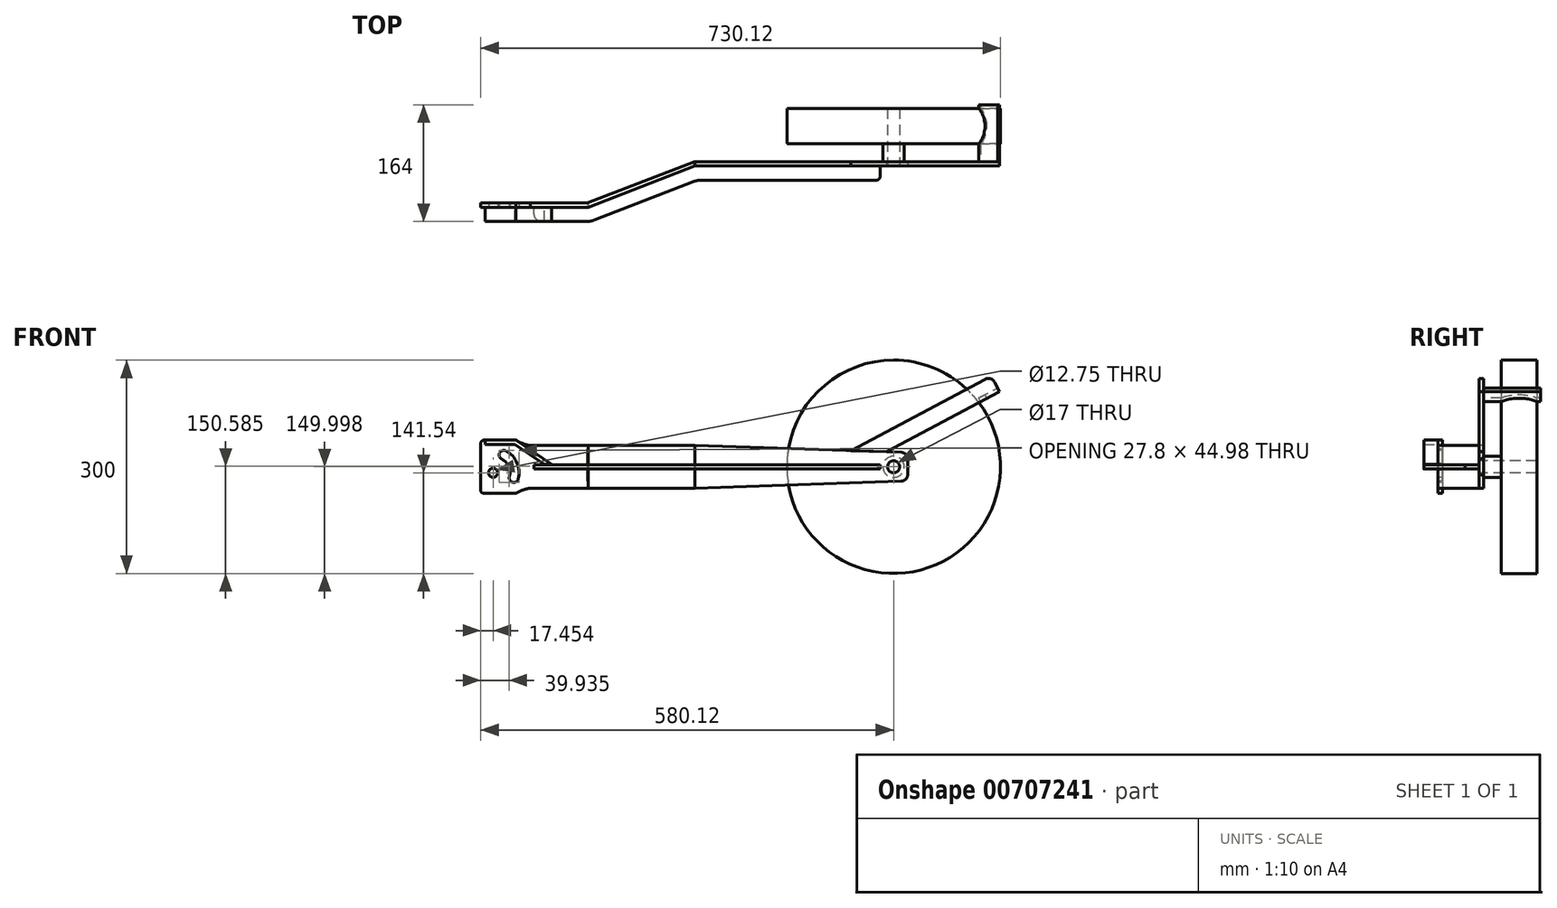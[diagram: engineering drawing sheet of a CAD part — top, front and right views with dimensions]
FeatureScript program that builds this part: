
annotation { "Feature Type Name" : "Feature", "Feature Type Description" : "" }
export const myFeature = defineFeature(function(context is Context, id is Id, definition is map)
    precondition{}
    {
        {
            var Q0;
            Q0=qCreatedBy(makeId("Top.planeOp"),FACE);
            var sketch = newSketch(context, id + "F0", { "sketchPlane" : qUnion([Q0])});
            skLineSegment(sketch, "E0", {"start": v(-300, 0) * mm, "end": v(300, 0) * mm, "construction": true});
            skLineSegment(sketch, "E1", {"start": v(-300, 0) * mm, "end": v(-150, 0) * mm});
            skLineSegment(sketch, "E2", {"start": v(-150, 0) * mm, "end": v(0, 58) * mm});
            skLineSegment(sketch, "E3", {"start": v(0, 58) * mm, "end": v(300, 58) * mm});
            skLineSegment(sketch, "E4", {"start": v(-300, 0) * mm, "end": v(-300, 128) * mm, "construction": true});
            skLineSegment(sketch, "E5", {"start": v(300, 0) * mm, "end": v(300, 128.18) * mm, "construction": true});
            skLineSegment(sketch, "E6.0", {"start": v(1.12, 52) * mm, "end": v(300.12, 52) * mm});
            skLineSegment(sketch, "E6.1", {"start": v(-148.88, -6) * mm, "end": v(1.12, 52) * mm});
            skLineSegment(sketch, "E6.2", {"start": v(-300, -6) * mm, "end": v(-148.88, -6) * mm});
            skLineSegment(sketch, "E7", {"start": v(-300, 0) * mm, "end": v(-300, -6) * mm});
            skLineSegment(sketch, "E8", {"start": v(300, 58) * mm, "end": v(300.12, 52) * mm});
            skLineSegment(sketch, "E9", {"start": v(-300, 33.9) * mm, "end": v(-300, 101.04) * mm});
            skSolve(sketch);
        }
        {
            var Q0;
            Q0 = qSketchRegion(id + "F0", true);
            extrude(context, id + "F1", {"entities" : qUnion([Q0]), "depth" : 60 * mm, "offsetDistance" : 25 * mm});
        }
        {
            var Q0;
            Q0=makeQuery(id+"F1.opExtrude","SWEPT_FACE",FACE,{"disambiguationData":[OSD([sQuery(id+"F0.wireOp",EDGE,"E6.2")])]});
            var sketch = newSketch(context, id + "F2", { "sketchPlane" : qUnion([Q0])});
            skLineSegment(sketch, "E10", {"start": v(-295, 67.5) * mm, "end": v(-250.3, 67.5) * mm});
            skPoint(sketch, "E11.visualSharp", {"position": v(-225, 67.5) * mm});
            skPoint(sketch, "E12.visualSharp", {"position": v(-225, -7.5) * mm});
            skPoint(sketch, "E13.visualSharp", {"position": v(-306, 67.5) * mm});
            skPoint(sketch, "E14.visualSharp", {"position": v(-300, -7.5) * mm});
            skPoint(sketch, "E15", {"position": v(-230, 60) * mm});
            skArc(sketch, "E16", {"start": v(-250.3, 67.5) * mm, "mid": v(-240.6, 62.51) * mm, "end": v(-230, 60) * mm});
            skPoint(sketch, "E17", {"position": v(-230, 0) * mm});
            skLineSegment(sketch, "E18", {"start": v(-230, 60) * mm, "end": v(-230, 0) * mm});
            skLineSegment(sketch, "E19", {"start": v(-148.88, 30) * mm, "end": v(-148.88, 30) * mm});
            skPoint(sketch, "E20.newPointA", {"position": v(-300, 67.5) * mm});
            skPoint(sketch, "E20.newPointB", {"position": v(-315.3, 67.5) * mm});
            skArc(sketch, "E20.filletArc", {"start": v(-295, 67.5) * mm, "mid": v(-298.54, 66.04) * mm, "end": v(-300, 62.5) * mm});
            skLineSegment(sketch, "E21", {"start": v(-240.6, 62.51) * mm, "end": v(-240.6, 0) * mm, "construction": true});
            skLineSegment(sketch, "E22.0", {"start": v(-300, 60) * mm, "end": v(-300, 0) * mm});
            skLineSegment(sketch, "E23", {"start": v(-300, 60) * mm, "end": v(-300, 62.5) * mm});
            skLineSegment(sketch, "E24", {"start": v(-300, 30) * mm, "end": v(-187.15, 30) * mm, "construction": true});
            skLineSegment(sketch, "E25.MirrorCS", {"start": v(-295, -7.5) * mm, "end": v(-250.3, -7.5) * mm});
            skArc(sketch, "E26.MirrorCS", {"start": v(-250.3, -7.5) * mm, "mid": v(-240.6, -2.51) * mm, "end": v(-230, 0) * mm});
            skArc(sketch, "E27.MirrorCS", {"start": v(-295, -7.5) * mm, "mid": v(-298.54, -6.04) * mm, "end": v(-300, -2.5) * mm});
            skLineSegment(sketch, "E28.MirrorCS", {"start": v(-300, 0) * mm, "end": v(-300, -2.5) * mm});
            skSolve(sketch);
        }
        {
            var Q0;
            Q0=makeQuery(id+"F1.opExtrude","SWEPT_FACE",FACE,{"disambiguationData":[OSD([sQuery(id+"F0.wireOp",EDGE,"E6.0")])]});
            var sketch = newSketch(context, id + "F3", { "sketchPlane" : qUnion([Q0])});
            skCircle(sketch, "E29", {"center": v(280.12, 30) * mm, "radius": 8.25 * mm});
            skPoint(sketch, "E29.centerSnap0", {"position": v(300.7, 30) * mm});
            skLineSegment(sketch, "E30", {"start": v(1.12, 60) * mm, "end": v(290.45, 50.32) * mm});
            skLineSegment(sketch, "E31", {"start": v(1.12, 0) * mm, "end": v(290.45, 9.68) * mm});
            skLineSegment(sketch, "E32", {"start": v(300.12, 40.33) * mm, "end": v(300.12, 19.67) * mm});
            skPoint(sketch, "E33.visualSharp", {"position": v(300.12, 50) * mm});
            skArc(sketch, "E33.filletArc", {"start": v(300.12, 40.33) * mm, "mid": v(297.3, 47.28) * mm, "end": v(290.45, 50.32) * mm});
            skPoint(sketch, "E34.visualSharp", {"position": v(300.12, 10) * mm});
            skArc(sketch, "E34.filletArc", {"start": v(290.45, 9.68) * mm, "mid": v(297.3, 12.72) * mm, "end": v(300.12, 19.67) * mm});
            skSolve(sketch);
        }
        {
            var Q0;
            {var subQ0=sQuery(id+"F3.wireOp",EDGE,"E30");Q0=makeQuery(id+"F3.imprint","IMPRINT",FACE,{"disambiguationData":[TD([[makeQuery(id+"F3.imprint","IMPRINT",EDGE,{"derivedFrom":subQ0}),1.0]])]});}
            var Q1;
            {var subQ0=sQuery(id+"F3.wireOp",EDGE,"E31");Q1=makeQuery(id+"F3.imprint","IMPRINT",FACE,{"disambiguationData":[TD([[makeQuery(id+"F3.imprint","IMPRINT",EDGE,{"derivedFrom":subQ0}),-1.0]])]});}
            var Q2;
            Q2=makeQuery(id+"F3.imprint","IMPRINT",FACE,{"disambiguationData":[TD([[makeQuery(id+"F3.imprint","IMPRINT",EDGE,{"derivedFrom":sQuery(id+"F3.wireOp",EDGE,"E29")}),1.0]])]});
            extrude(context, id + "F4", {"entities" : qUnion([Q0, Q1, Q2]), "operationType" : NewBodyOperationType.REMOVE, "oppositeDirection" : true, "depth" : 25 * mm, "offsetDistance" : 25 * mm});
        }
        {
            var Q0;
            Q0=makeQuery(id+"F2.imprint","IMPRINT",FACE,{"disambiguationData":[TD([[makeQuery(id+"F2.imprint","IMPRINT",EDGE,{"derivedFrom":sQuery(id+"F2.wireOp",EDGE,"E10")}),-1.0]])]});
            var Q1;
            Q1=makeQuery(id+"F2.imprint","IMPRINT",FACE,{"disambiguationData":[TD([[makeQuery(id+"F2.imprint","IMPRINT",EDGE,{"derivedFrom":sQuery(id+"F2.wireOp",EDGE,"6MBA5zCG-kA5Y-AlUf-X3c2-cWm0OstjSN9L")}),1.0]])]});
            extrude(context, id + "F5", {"entities" : qUnion([Q0, Q1]), "operationType" : NewBodyOperationType.ADD, "oppositeDirection" : true, "depth" : 6 * mm, "offsetDistance" : 25 * mm});
        }
        {
            var Q0;
            {var subQ0=sQuery(id+"F0.wireOp",EDGE,"E6.2");Q0=makeQuery(id+"F5.boolean.opBoolean","MERGE",FACE,{"derivedFrom":[makeQuery(id+"F1.opExtrude","SWEPT_FACE",FACE,{"disambiguationData":[OSD([subQ0])]}),makeQuery(id+"F5.opExtrude","CAP_FACE",FACE,{"disambiguationData":[OSD([subQ0,sQuery(id+"F2.wireOp",EDGE,"2KIgmFb8-dbBe-8aPb-DhG4-cKlgFUq4y2h1"),sQuery(id+"F2.wireOp",EDGE,"6MBA5zCG-kA5Y-AlUf-X3c2-cWm0OstjSN9L"),sQuery(id+"F2.wireOp",EDGE,"E14.filletArc"),sQuery(id+"F2.wireOp",EDGE,"07031323-947f-4b0b-b8ee-12b4b9ee6c110.MirrorCS")])],"isStart":true}),makeQuery(id+"F5.opExtrude","CAP_FACE",FACE,{"disambiguationData":[OSD([subQ0,sQuery(id+"F2.wireOp",EDGE,"E10"),sQuery(id+"F2.wireOp",EDGE,"E16"),sQuery(id+"F2.wireOp",EDGE,"2cHqhizW-JMVK-h9AF-USdZ-6RG1NBp1Brja"),sQuery(id+"F2.wireOp",EDGE,"E20.filletArc")])],"isStart":true})]});}
            var sketch = newSketch(context, id + "F6", { "sketchPlane" : qUnion([Q0])});
            skPoint(sketch, "E35.centerSnap0", {"position": v(-303.27, 27.75) * mm});
            skPoint(sketch, "E35.centerSnap1", {"position": v(-270.79, 64.03) * mm});
            skLineSegment(sketch, "E36", {"start": v(-271.04, 55.82) * mm, "end": v(-250.9, 3.47) * mm, "construction": true});
            skPoint(sketch, "E37.orphan", {"position": v(-256.1, 1.25) * mm});
            skLineSegment(sketch, "E38", {"start": v(-289.53, 18.87) * mm, "end": v(-224.13, 44.01) * mm, "construction": true});
            skPoint(sketch, "E39.center.orphan", {"position": v(-270.79, 26.53) * mm});
            skPoint(sketch, "E40.0.endCap.center.orphan", {"position": v(-269.46, 51.72) * mm});
            skPoint(sketch, "E40.0.left.start.orphan", {"position": v(-253.42, 14.54) * mm});
            skPoint(sketch, "E40.0.startCap.center.orphan", {"position": v(-252.07, 6.49) * mm});
            skPoint(sketch, "E41", {"position": v(-267.5, 46.62) * mm});
            skPoint(sketch, "E42", {"position": v(-256.25, 17.37) * mm});
            skArc(sketch, "E43", {"start": v(-253.42, 14.54) * mm, "mid": v(-254.95, 33) * mm, "end": v(-267.5, 46.62) * mm});
            skArc(sketch, "E44.0.startCap", {"start": v(-247.12, 12.94) * mm, "mid": v(-255.02, 8.24) * mm, "end": v(-259.72, 16.13) * mm});
            skArc(sketch, "E44.0.endCap", {"start": v(-270.59, 40.9) * mm, "mid": v(-273.22, 49.7) * mm, "end": v(-264.41, 52.34) * mm});
            skArc(sketch, "E44.0.left", {"start": v(-259.72, 16.13) * mm, "mid": v(-260.9, 30.39) * mm, "end": v(-270.59, 40.9) * mm});
            skArc(sketch, "E44.0.right", {"start": v(-247.12, 12.94) * mm, "mid": v(-249, 35.6) * mm, "end": v(-264.41, 52.34) * mm});
            skCircle(sketch, "E45", {"center": v(-282.55, 21.55) * mm, "radius": 6.38 * mm});
            skSolve(sketch);
        }
        {
            var Q0;
            Q0 = qSketchRegion(id + "F6", true);
            extrude(context, id + "F7", {"entities" : qUnion([Q0]), "operationType" : NewBodyOperationType.REMOVE, "oppositeDirection" : true, "depth" : 25 * mm, "offsetDistance" : 25 * mm});
        }
        {
            var Q0;
            Q0=makeQuery(id+"F1.opExtrude","CAP_FACE",FACE,{"disambiguationData":[OSD([sQuery(id+"F0.wireOp",EDGE,"E1"),sQuery(id+"F0.wireOp",EDGE,"E2"),sQuery(id+"F0.wireOp",EDGE,"E3"),sQuery(id+"F0.wireOp",EDGE,"E6.0"),sQuery(id+"F0.wireOp",EDGE,"E6.1"),sQuery(id+"F0.wireOp",EDGE,"E6.2"),sQuery(id+"F0.wireOp",EDGE,"E7"),sQuery(id+"F0.wireOp",EDGE,"E8")])],"isStart":true});
            cPlane(context, id + "F8", {"entities" : qUnion([Q0]), "cplaneType" : CPlaneType.OFFSET, "offset" : 33 * mm, "oppositeDirection" : true, "width" : 150 * mm, "height" : 150 * mm});
        }
        {
            var Q0;
            Q0=qCreatedBy(id+"F8.planeOp",FACE);
            var sketch = newSketch(context, id + "F9", { "sketchPlane" : qUnion([Q0])});
            skLineSegment(sketch, "E46.0", {"start": v(-225.15, 6) * mm, "end": v(-148.88, 6) * mm});
            skLineSegment(sketch, "E47.0", {"start": v(-148.88, 6) * mm, "end": v(1.12, -52) * mm});
            skLineSegment(sketch, "E48.0", {"start": v(-140.8, 24.32) * mm, "end": v(0.5, -30.32) * mm});
            skLineSegment(sketch, "E48.1", {"start": v(-215.15, 26) * mm, "end": v(-149.81, 26) * mm});
            skLineSegment(sketch, "E49", {"start": v(-225.15, 16) * mm, "end": v(-225.15, 6) * mm});
            skLineSegment(sketch, "E50", {"start": v(1.12, -52) * mm, "end": v(261.12, -52) * mm});
            skLineSegment(sketch, "E51.0", {"start": v(9.52, -32) * mm, "end": v(256.12, -32) * mm});
            skLineSegment(sketch, "E52", {"start": v(261.12, -37) * mm, "end": v(261.12, -52) * mm});
            skPoint(sketch, "E53.visualSharp", {"position": v(-225.15, 26) * mm});
            skArc(sketch, "E53.filletArc", {"start": v(-215.15, 26) * mm, "mid": v(-222.22, 23.07) * mm, "end": v(-225.15, 16) * mm});
            skPoint(sketch, "E54.visualSharp", {"position": v(261.12, -32) * mm});
            skArc(sketch, "E54.filletArc", {"start": v(261.12, -37) * mm, "mid": v(259.66, -33.46) * mm, "end": v(256.12, -32) * mm});
            skPoint(sketch, "E55.visualSharp", {"position": v(-145.15, 26) * mm});
            skArc(sketch, "E55.filletArc", {"start": v(-140.8, 24.32) * mm, "mid": v(-145.23, 25.58) * mm, "end": v(-149.81, 26) * mm});
            skPoint(sketch, "E56.visualSharp", {"position": v(4.85, -32) * mm});
            skArc(sketch, "E56.filletArc", {"start": v(0.5, -30.32) * mm, "mid": v(4.93, -31.58) * mm, "end": v(9.52, -32) * mm});
            skSolve(sketch);
        }
        {
            var Q0;
            Q0 = qSketchRegion(id + "F9", true);
            extrude(context, id + "F10", {"entities" : qUnion([Q0]), "depth" : 6 * mm, "offsetDistance" : 25 * mm});
        }
        {
            var Q0;
            Q0 = qSketchRegion(id + "F2", true);
            extrude(context, id + "F11", {"entities" : qUnion([Q0]), "operationType" : NewBodyOperationType.ADD, "oppositeDirection" : true, "depth" : 6 * mm, "offsetDistance" : 25 * mm});
        }
        {
            var Q0;
            Q0 = qSketchRegion(id + "F6", true);
            extrude(context, id + "F12", {"entities" : qUnion([Q0]), "operationType" : NewBodyOperationType.REMOVE, "oppositeDirection" : true, "depth" : 25 * mm, "offsetDistance" : 25 * mm});
        }
        {
            var Q0;
            Q0 = qSketchRegion(id + "F6", true);
            extrude(context, id + "F13", {"entities" : qUnion([Q0]), "operationType" : NewBodyOperationType.REMOVE, "oppositeDirection" : true, "depth" : 25 * mm, "offsetDistance" : 25 * mm});
        }
        {
            var Q0;
            {var subQ0=sQuery(id+"F2.wireOp",EDGE,"E18");Q0=makeQuery(id+"F2.imprint","IMPRINT",FACE,{"disambiguationData":[TD([[makeQuery(id+"F2.imprint","IMPRINT",EDGE,{"derivedFrom":subQ0}),1.0]])]});}
            var sketch = newSketch(context, id + "F14", { "sketchPlane" : qUnion([Q0])});
            skLineSegment(sketch, "E57.0", {"start": v(-148.88, 55) * mm, "end": v(-148.88, 35) * mm});
            skLineSegment(sketch, "E58", {"start": v(-150.92, 10) * mm, "end": v(-146.58, 10) * mm, "construction": true});
            skLineSegment(sketch, "E59", {"start": v(-148.88, 30) * mm, "end": v(-146.58, 30) * mm, "construction": true});
            skLineSegment(sketch, "E60", {"start": v(-148.88, 35) * mm, "end": v(-143.51, 35) * mm, "construction": true});
            skLineSegment(sketch, "E61", {"start": v(-147.72, 25) * mm, "end": v(-151.64, 25) * mm, "construction": true});
            skPoint(sketch, "E62.orphan", {"position": v(-148.88, 60) * mm});
            skLineSegment(sketch, "E63.trimOffspring", {"start": v(-148.88, 25) * mm, "end": v(-148.88, 10) * mm});
            skPoint(sketch, "E64.orphan", {"position": v(-148.88, 0) * mm});
            skLineSegment(sketch, "E65.0", {"start": v(-149.88, 25) * mm, "end": v(-149.88, 10) * mm});
            skLineSegment(sketch, "E66.0", {"start": v(-149.88, 55) * mm, "end": v(-149.88, 35) * mm});
            skLineSegment(sketch, "E67", {"start": v(-149.88, 35) * mm, "end": v(-148.88, 35) * mm});
            skLineSegment(sketch, "E68", {"start": v(-149.88, 55) * mm, "end": v(-148.88, 55) * mm});
            skLineSegment(sketch, "E69", {"start": v(-149.88, 10) * mm, "end": v(-148.88, 10) * mm});
            skLineSegment(sketch, "E70", {"start": v(-149.88, 25) * mm, "end": v(-148.88, 25) * mm});
            skPoint(sketch, "E71.end.orphan", {"position": v(-146.58, 55) * mm});
            skSolve(sketch);
        }
        {
            var Q0;
            Q0 = qSketchRegion(id + "F14", true);
            extrude(context, id + "F15", {"entities" : qUnion([Q0]), "operationType" : NewBodyOperationType.REMOVE, "oppositeDirection" : true, "depth" : 25 * mm, "offsetDistance" : 25 * mm});
        }
        {
            var Q0;
            {var subQ0=sQuery(id+"F2.wireOp",EDGE,"E23");var subQ1=sQuery(id+"F2.wireOp",EDGE,"E20.filletArc");var subQ2=sQuery(id+"F2.wireOp",EDGE,"E16");var subQ3=sQuery(id+"F2.wireOp",EDGE,"E10");var subQ4=sQuery(id+"F0.wireOp",EDGE,"E6.2");Q0=makeQuery(id+"F11.boolean.opBoolean","MERGE",FACE,{"derivedFrom":[makeQuery(id+"F5.boolean.opBoolean","MERGE",FACE,{"derivedFrom":[makeQuery(id+"F1.opExtrude","SWEPT_FACE",FACE,{"disambiguationData":[OSD([subQ4])]}),makeQuery(id+"F5.opExtrude","CAP_FACE",FACE,{"disambiguationData":[OSD([subQ4,subQ3,subQ2,subQ1,subQ0])],"isStart":true})]}),makeQuery(id+"F11.opExtrude","CAP_FACE",FACE,{"disambiguationData":[OSD([subQ3,subQ2,sQuery(id+"F2.wireOp",EDGE,"E18"),subQ1,sQuery(id+"F2.wireOp",EDGE,"E22.0"),subQ0,sQuery(id+"F2.wireOp",EDGE,"E25.MirrorCS"),sQuery(id+"F2.wireOp",EDGE,"E26.MirrorCS"),sQuery(id+"F2.wireOp",EDGE,"E27.MirrorCS"),sQuery(id+"F2.wireOp",EDGE,"E28.MirrorCS")])],"isStart":true})]});}
            var sketch = newSketch(context, id + "F16", { "sketchPlane" : qUnion([Q0])});
            skLineSegment(sketch, "E72", {"start": v(-294.02, 67.5) * mm, "end": v(-250.3, 67.5) * mm});
            skLineSegment(sketch, "E73", {"start": v(-250.3, 67.5) * mm, "end": v(-200.12, 33.41) * mm});
            skLineSegment(sketch, "E74.0", {"start": v(-252.15, 61.5) * mm, "end": v(-210.8, 33.41) * mm});
            skLineSegment(sketch, "E74.1", {"start": v(-294.02, 61.5) * mm, "end": v(-252.15, 61.5) * mm});
            skLineSegment(sketch, "E75", {"start": v(-294.02, 67.5) * mm, "end": v(-294.02, 61.5) * mm});
            skLineSegment(sketch, "E76", {"start": v(-200.12, 33.41) * mm, "end": v(-210.8, 33.41) * mm});
            skSolve(sketch);
        }
        {
            var Q0;
            Q0 = qSketchRegion(id + "F16", true);
            extrude(context, id + "F17", {"entities" : qUnion([Q0]), "depth" : 20 * mm, "offsetDistance" : 25 * mm});
        }
        {
            var Q0;
            Q0=makeQuery(id+"F1.opExtrude","SWEPT_FACE",FACE,{"disambiguationData":[OSD([sQuery(id+"F0.wireOp",EDGE,"E3")])]});
            var sketch = newSketch(context, id + "F18", { "sketchPlane" : qUnion([Q0])});
            skCircle(sketch, "E77", {"center": v(-280.12, 30) * mm, "radius": 15 * mm});
            skSolve(sketch);
        }
        {
            var Q0;
            Q0 = qSketchRegion(id + "F18", true);
            extrude(context, id + "F19", {"entities" : qUnion([Q0]), "operationType" : NewBodyOperationType.ADD, "depth" : 25 * mm, "offsetDistance" : 25 * mm});
        }
        {
            var Q0;
            Q0=makeQuery(id+"F19.opExtrude","CAP_FACE",FACE,{"disambiguationData":[OSD([sQuery(id+"F18.wireOp",EDGE,"E77")])],"isStart":false});
            var sketch = newSketch(context, id + "F20", { "sketchPlane" : qUnion([Q0])});
            skCircle(sketch, "E78", {"center": v(-280.12, 30) * mm, "radius": 150 * mm});
            skArc(sketch, "E79", {"start": v(-200.98, 137.3) * mm, "mid": v(-249.03, 170.23) * mm, "end": v(-306.82, 177.61) * mm});
            skSolve(sketch);
        }
        {
            var Q0;
            Q0 = qSketchRegion(id + "F20", true);
            extrude(context, id + "F21", {"entities" : qUnion([Q0]), "operationType" : NewBodyOperationType.ADD, "depth" : 50 * mm, "offsetDistance" : 25 * mm});
        }
        {
            var Q0;
            Q0=makeQuery(id+"F1.opExtrude","SWEPT_FACE",FACE,{"disambiguationData":[OSD([sQuery(id+"F0.wireOp",EDGE,"E6.0")])]});
            var sketch = newSketch(context, id + "F22", { "sketchPlane" : qUnion([Q0])});
            skLineSegment(sketch, "E80", {"start": v(428.93, 135.74) * mm, "end": v(421.86, 148.98) * mm});
            skLineSegment(sketch, "E81", {"start": v(428.93, 135.74) * mm, "end": v(270.12, 51) * mm});
            skLineSegment(sketch, "E82", {"start": v(270.12, 51) * mm, "end": v(220.15, 52.67) * mm});
            skLineSegment(sketch, "E83", {"start": v(220.15, 52.67) * mm, "end": v(408.33, 153.1) * mm});
            skPoint(sketch, "E84.visualSharp", {"position": v(417.16, 157.8) * mm});
            skArc(sketch, "E84.filletArc", {"start": v(421.86, 148.98) * mm, "mid": v(415.95, 153.84) * mm, "end": v(408.33, 153.1) * mm});
            skPoint(sketch, "E85.orphan", {"position": v(431.28, 131.33) * mm});
            skSolve(sketch);
        }
        {
            var Q0;
            Q0 = qSketchRegion(id + "F22", true);
            extrude(context, id + "F23", {"entities" : qUnion([Q0]), "oppositeDirection" : true, "depth" : 6 * mm, "offsetDistance" : 25 * mm});
        }
        {
            var Q0;
            Q0=makeQuery(id+"F23.opExtrude","CAP_FACE",FACE,{"disambiguationData":[OSD([sQuery(id+"F22.wireOp",EDGE,"E80"),sQuery(id+"F22.wireOp",EDGE,"E81"),sQuery(id+"F22.wireOp",EDGE,"E82"),sQuery(id+"F22.wireOp",EDGE,"E83"),sQuery(id+"F22.wireOp",EDGE,"E84.filletArc")])],"isStart":false});
            var sketch = newSketch(context, id + "F24", { "sketchPlane" : qUnion([Q0])});
            skLineSegment(sketch, "E86", {"start": v(-428.93, 135.74) * mm, "end": v(-402.46, 121.62) * mm});
            skLineSegment(sketch, "E87", {"start": v(-402.46, 121.62) * mm, "end": v(-399.63, 126.91) * mm});
            skLineSegment(sketch, "E88", {"start": v(-399.63, 126.91) * mm, "end": v(-426.1, 141.04) * mm});
            skLineSegment(sketch, "E89", {"start": v(-426.1, 141.04) * mm, "end": v(-428.93, 135.74) * mm});
            skSolve(sketch);
        }
        {
            var Q0;
            Q0 = qSketchRegion(id + "F24", true);
            extrude(context, id + "F25", {"entities" : qUnion([Q0]), "depth" : 80 * mm, "offsetDistance" : 25 * mm});
        }
        {
            var Q0;
            Q0=makeQuery(id+"F25.opExtrude","SWEPT_FACE",FACE,{"disambiguationData":[OSD([sQuery(id+"F24.wireOp",EDGE,"E88")])]});
            var sketch = newSketch(context, id + "F26", { "sketchPlane" : qUnion([Q0])});
            skArc(sketch, "E90", {"start": v(412.33, 83) * mm, "mid": v(422.33, 108) * mm, "end": v(412.33, 133) * mm});
            skSolve(sketch);
        }
        {
            var Q0;
            Q0 = qSketchRegion(id + "F26", true);
            var Q1;
            {var subQ0=sQuery(id+"F26.wireOp",EDGE,"E90");Q1=makeQuery(id+"F26.imprint","IMPRINT",FACE,{"disambiguationData":[TD([[makeQuery(id+"F26.imprint","IMPRINT",EDGE,{"derivedFrom":subQ0}),1.0]])]});}
            extrude(context, id + "F27", {"entities" : qUnion([Q0, Q1]), "operationType" : NewBodyOperationType.REMOVE, "oppositeDirection" : true, "depth" : 25 * mm, "offsetDistance" : 25 * mm});
        }
        {
            var Q0;
            Q0=makeQuery(id+"F1.opExtrude","SWEPT_FACE",FACE,{"disambiguationData":[OSD([sQuery(id+"F0.wireOp",EDGE,"E6.0")])]});
            var sketch = newSketch(context, id + "F28", { "sketchPlane" : qUnion([Q0])});
            skCircle(sketch, "E91", {"center": v(280.12, 30) * mm, "radius": 8.5 * mm});
            skSolve(sketch);
        }
        {
            var Q0;
            Q0 = qSketchRegion(id + "F28", true);
            extrude(context, id + "F29", {"entities" : qUnion([Q0]), "operationType" : NewBodyOperationType.REMOVE, "endBound" : BoundingType.THROUGH_ALL, "oppositeDirection" : true, "depth" : 25 * mm, "offsetDistance" : 25 * mm});
        }
    });
